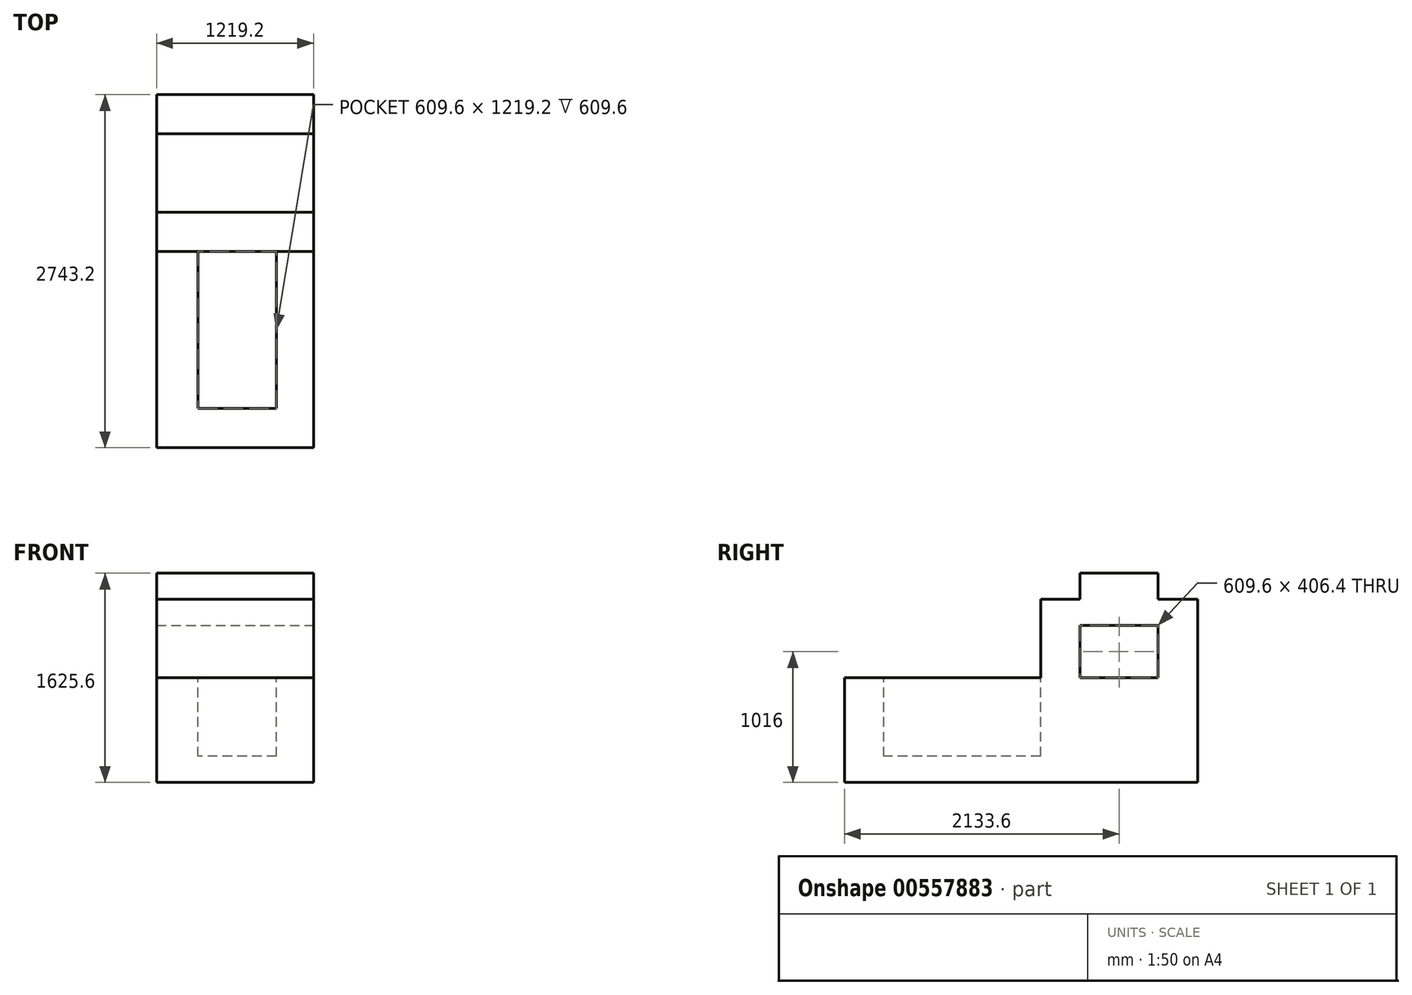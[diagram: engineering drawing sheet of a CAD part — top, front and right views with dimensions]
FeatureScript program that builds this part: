
annotation { "Feature Type Name" : "Feature", "Feature Type Description" : "" }
export const myFeature = defineFeature(function(context is Context, id is Id, definition is map)
    precondition{}
    {
        {
            var Q0;
            Q0=qCreatedBy(makeId("Front.planeOp"),FACE);
            var sketch = newSketch(context, id + "F0", { "sketchPlane" : qUnion([Q0])});
            skLineSegment(sketch, "E0", {"start": v(-322.75, -75.61) * mm, "end": v(896.45, -75.61) * mm});
            skLineSegment(sketch, "E1", {"start": v(896.45, -75.61) * mm, "end": v(896.45, 737.19) * mm});
            skLineSegment(sketch, "E2", {"start": v(896.45, 737.19) * mm, "end": v(-322.75, 737.19) * mm});
            skLineSegment(sketch, "E3", {"start": v(-322.75, 737.19) * mm, "end": v(-322.75, -75.61) * mm});
            skSolve(sketch);
        }
        {
            var Q0;
            Q0=makeQuery(id+"F0.imprint","IMPRINT",FACE,{"disambiguationData":[TD([[makeQuery(id+"F0.imprint","IMPRINT",EDGE,{"derivedFrom":sQuery(id+"F0.wireOp",EDGE,"E0")}),1.0]])]});
            extrude(context, id + "F1", {"entities" : qUnion([Q0]), "oppositeDirection" : true, "depth" : 1524 * mm, "offsetDistance" : 25.4 * mm});
        }
        {
            var Q0;
            Q0=makeQuery(id+"F1.opExtrude","SWEPT_FACE",FACE,{"disambiguationData":[OSD([sQuery(id+"F0.wireOp",EDGE,"E1")])]});
            var sketch = newSketch(context, id + "F2", { "sketchPlane" : qUnion([Q0])});
            skLineSegment(sketch, "E4", {"start": v(1524, -75.61) * mm, "end": v(1524, 1346.79) * mm});
            skLineSegment(sketch, "E5", {"start": v(1524, 1346.79) * mm, "end": v(1828.8, 1346.79) * mm});
            skLineSegment(sketch, "E6", {"start": v(1828.8, 1346.79) * mm, "end": v(1828.8, 1549.99) * mm});
            skLineSegment(sketch, "E7", {"start": v(1828.8, 1549.99) * mm, "end": v(2438.4, 1549.99) * mm});
            skLineSegment(sketch, "E8", {"start": v(2438.4, 1549.99) * mm, "end": v(2438.4, 1346.79) * mm});
            skLineSegment(sketch, "E9", {"start": v(2438.4, 1346.79) * mm, "end": v(2743.2, 1346.79) * mm});
            skLineSegment(sketch, "E10", {"start": v(2743.2, 1346.79) * mm, "end": v(2743.2, -75.61) * mm});
            skLineSegment(sketch, "E11", {"start": v(2743.2, -75.61) * mm, "end": v(1524, -75.61) * mm});
            skSolve(sketch);
        }
        {
            var Q0;
            {var subQ0=sQuery(id+"F2.wireOp",EDGE,"E5");Q0=makeQuery(id+"F2.imprint","IMPRINT",FACE,{"disambiguationData":[TD([[makeQuery(id+"F2.imprint","IMPRINT",EDGE,{"derivedFrom":subQ0}),-1.0]])]});}
            extrude(context, id + "F3", {"entities" : qUnion([Q0]), "operationType" : NewBodyOperationType.ADD, "oppositeDirection" : true, "depth" : 1219.2 * mm, "offsetDistance" : 25.4 * mm});
        }
        {
            var Q0;
            Q0=makeQuery(id+"F3.boolean.opBoolean","MERGE",FACE,{"derivedFrom":[makeQuery(id+"F1.opExtrude","SWEPT_FACE",FACE,{"disambiguationData":[OSD([sQuery(id+"F0.wireOp",EDGE,"E1")])]}),makeQuery(id+"F3.opExtrude","CAP_FACE",FACE,{"disambiguationData":[OSD([sQuery(id+"F2.wireOp",EDGE,"E4"),sQuery(id+"F2.wireOp",EDGE,"E5"),sQuery(id+"F2.wireOp",EDGE,"E6"),sQuery(id+"F2.wireOp",EDGE,"E7"),sQuery(id+"F2.wireOp",EDGE,"E8"),sQuery(id+"F2.wireOp",EDGE,"E9"),sQuery(id+"F2.wireOp",EDGE,"E10"),sQuery(id+"F2.wireOp",EDGE,"E11")])],"isStart":true})]});
            var sketch = newSketch(context, id + "F4", { "sketchPlane" : qUnion([Q0])});
            skSolve(sketch);
        }
        {
            var Q0;
            {var subQ0=sQuery(id+"F0.wireOp",EDGE,"E1");Q0=makeQuery(id+"F4.imprint","IMPRINT",FACE,{"disambiguationData":[TD([[makeQuery(id+"F4.imprint","IMPRINT",EDGE,{"derivedFrom":makeQuery(id+"F1.opExtrude","CAP_EDGE",EDGE,{"disambiguationData":[OSD([subQ0])],"isStart":true})}),-1.0]])]});}
            var sketch = newSketch(context, id + "F5", { "sketchPlane" : qUnion([Q0])});
            skLineSegment(sketch, "E12.bottom", {"start": v(1828.8, 1143.59) * mm, "end": v(2438.4, 1143.59) * mm});
            skLineSegment(sketch, "E12.top", {"start": v(1828.8, 737.19) * mm, "end": v(2438.4, 737.19) * mm});
            skLineSegment(sketch, "E12.left", {"start": v(1828.8, 1143.59) * mm, "end": v(1828.8, 737.19) * mm});
            skLineSegment(sketch, "E12.right", {"start": v(2438.4, 1143.59) * mm, "end": v(2438.4, 737.19) * mm});
            skSolve(sketch);
        }
        {
            var Q0;
            Q0 = qSketchRegion(id + "F5", true);
            extrude(context, id + "F6", {"entities" : qUnion([Q0]), "operationType" : NewBodyOperationType.REMOVE, "endBound" : BoundingType.THROUGH_ALL, "oppositeDirection" : true, "depth" : 25.4 * mm, "offsetDistance" : 25.4 * mm});
        }
        {
            var Q0;
            Q0=makeQuery(id+"F1.opExtrude","SWEPT_FACE",FACE,{"disambiguationData":[OSD([sQuery(id+"F0.wireOp",EDGE,"E2")])]});
            var sketch = newSketch(context, id + "F7", { "sketchPlane" : qUnion([Q0])});
            skLineSegment(sketch, "E13", {"start": v(-322.75, 1524) * mm, "end": v(0, 1524) * mm});
            skLineSegment(sketch, "E14", {"start": v(0, 1524) * mm, "end": v(0, 304.8) * mm});
            skLineSegment(sketch, "E15", {"start": v(0, 304.8) * mm, "end": v(609.6, 304.8) * mm});
            skLineSegment(sketch, "E16", {"start": v(609.6, 304.8) * mm, "end": v(609.6, 1524) * mm});
            skSolve(sketch);
        }
        {
            var Q0;
            {var subQ0=sQuery(id+"F7.wireOp",EDGE,"E14");Q0=makeQuery(id+"F7.imprint","IMPRINT",FACE,{"disambiguationData":[TD([[makeQuery(id+"F7.imprint","IMPRINT",EDGE,{"derivedFrom":subQ0}),1.0]])]});}
            extrude(context, id + "F8", {"entities" : qUnion([Q0]), "operationType" : NewBodyOperationType.REMOVE, "depth" : 609.6 * mm, "offsetDistance" : 25.4 * mm});
        }
        {
            var Q0;
            {var subQ0=sQuery(id+"F7.wireOp",EDGE,"E14");Q0=makeQuery(id+"F7.imprint","IMPRINT",FACE,{"disambiguationData":[TD([[makeQuery(id+"F7.imprint","IMPRINT",EDGE,{"derivedFrom":subQ0}),1.0]])]});}
            extrude(context, id + "F9", {"entities" : qUnion([Q0]), "operationType" : NewBodyOperationType.ADD, "oppositeDirection" : true, "depth" : 609.6 * mm, "offsetDistance" : 25.4 * mm});
        }
        {
            var Q0;
            {var subQ0=sQuery(id+"F7.wireOp",EDGE,"E14");Q0=makeQuery(id+"F7.imprint","IMPRINT",FACE,{"disambiguationData":[TD([[makeQuery(id+"F7.imprint","IMPRINT",EDGE,{"derivedFrom":subQ0}),1.0]])]});}
            extrude(context, id + "F10", {"entities" : qUnion([Q0]), "operationType" : NewBodyOperationType.REMOVE, "oppositeDirection" : true, "depth" : 609.6 * mm, "offsetDistance" : 25.4 * mm});
        }
    });
